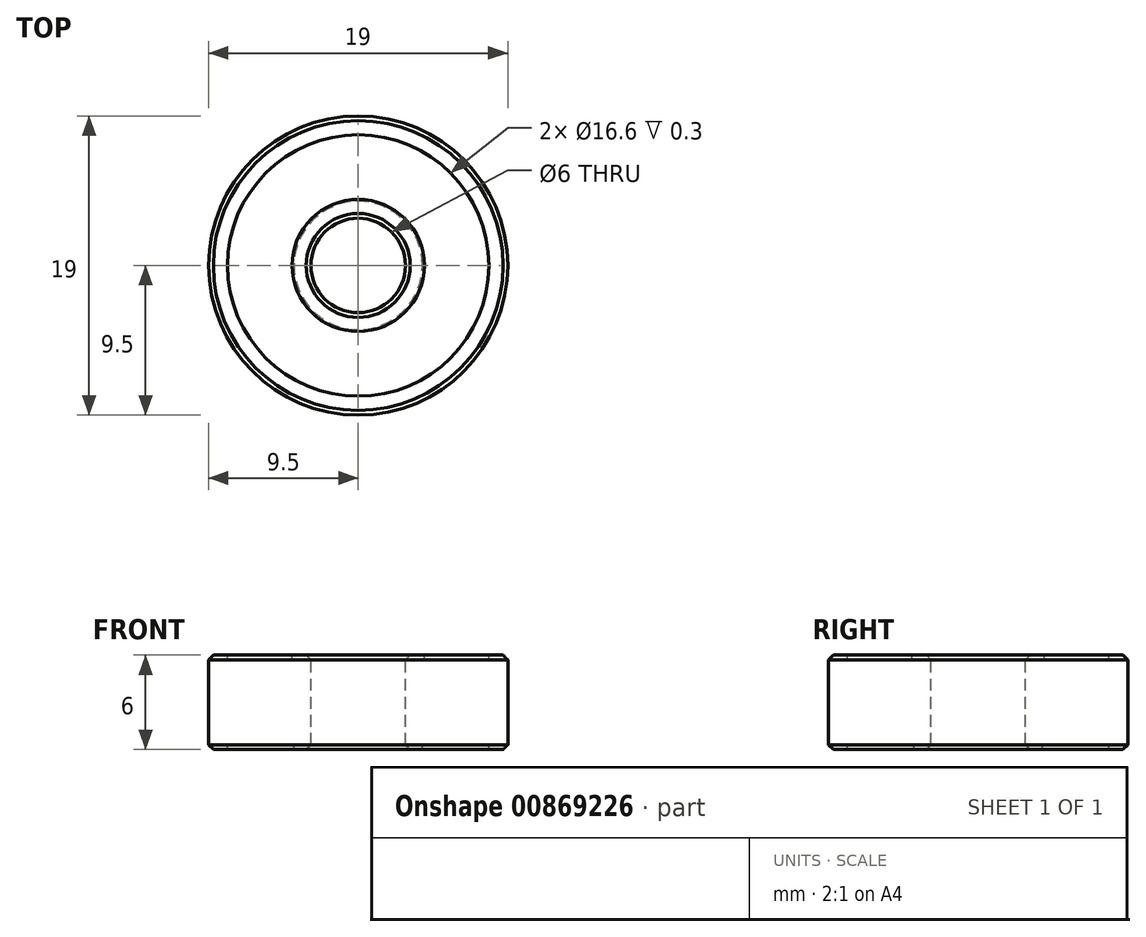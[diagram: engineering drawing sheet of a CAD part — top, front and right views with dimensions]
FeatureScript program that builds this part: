
annotation { "Feature Type Name" : "Feature", "Feature Type Description" : "" }
export const myFeature = defineFeature(function(context is Context, id is Id, definition is map)
    precondition{}
    {
        {
            var Q0;
            Q0=qCreatedBy(makeId("Front.planeOp"),FACE);
            var sketch = newSketch(context, id + "F0", { "sketchPlane" : qUnion([Q0])});
            skLineSegment(sketch, "E0.bottom", {"start": v(3, 3) * mm, "end": v(9.5, 3) * mm});
            skLineSegment(sketch, "E0.top", {"start": v(3, -3) * mm, "end": v(9.5, -3) * mm});
            skLineSegment(sketch, "E0.left", {"start": v(3, 3) * mm, "end": v(3, -3) * mm});
            skLineSegment(sketch, "E0.right", {"start": v(9.5, 3) * mm, "end": v(9.5, -3) * mm});
            skLineSegment(sketch, "E1", {"start": v(0, 3) * mm, "end": v(0, -3) * mm, "construction": true});
            skLineSegment(sketch, "E2", {"start": v(4.2, 3) * mm, "end": v(4.2, 2.7) * mm});
            skLineSegment(sketch, "E3", {"start": v(4.2, 2.7) * mm, "end": v(8.3, 2.7) * mm});
            skLineSegment(sketch, "E4", {"start": v(8.3, 2.7) * mm, "end": v(8.3, 3) * mm});
            skLineSegment(sketch, "E5", {"start": v(4.08, -3) * mm, "end": v(4.08, -2.7) * mm});
            skLineSegment(sketch, "E6", {"start": v(4.08, -2.7) * mm, "end": v(8.3, -2.7) * mm});
            skLineSegment(sketch, "E7", {"start": v(8.3, -2.7) * mm, "end": v(8.3, -3) * mm});
            skSolve(sketch);
        }
        {
            var Q0;
            {var subQ3=sQuery(id+"F0.wireOp",EDGE,"E0.left");Q0=makeQuery(id+"F0.imprint","IMPRINT",FACE,{"disambiguationData":[TD([[makeQuery(id+"F0.imprint","IMPRINT",EDGE,{"derivedFrom":subQ3}),1.0]])]});}
            var Q1;
            Q1=sQuery(id+"F0.wireOp",EDGE,"E1");
            revolve(context, id + "F1", {"surfaceOperationType" : NewSurfaceOperationType.NEW, "entities" : qUnion([Q0]), "axis" : qUnion([Q1]), "revolveType" : RevolveType.FULL});
        }
        {
            var Q0;
            Q0=makeQuery(id+"F1.opRevolve","SWEPT_EDGE",EDGE,{"disambiguationData":[OSD([sQuery(id+"F0.wireOp",EDGE,"E0.bottom"),sQuery(id+"F0.wireOp",EDGE,"E0.right")])]});
            var Q1;
            Q1=makeQuery(id+"F1.opRevolve","SWEPT_EDGE",EDGE,{"disambiguationData":[OSD([sQuery(id+"F0.wireOp",EDGE,"E0.top"),sQuery(id+"F0.wireOp",EDGE,"E0.right")])]});
            var Q2;
            Q2=makeQuery(id+"F1.opRevolve","SWEPT_EDGE",EDGE,{"disambiguationData":[OSD([sQuery(id+"F0.wireOp",EDGE,"E0.bottom"),sQuery(id+"F0.wireOp",EDGE,"E0.left")])]});
            var Q3;
            Q3=makeQuery(id+"F1.opRevolve","SWEPT_EDGE",EDGE,{"disambiguationData":[OSD([sQuery(id+"F0.wireOp",EDGE,"E0.top"),sQuery(id+"F0.wireOp",EDGE,"E0.left")])]});
            chamfer(context, id + "F2", {"entities" : qUnion([Q0, Q1, Q2, Q3]), "width" : 0.3 * mm, "tangentPropagation" : true});
        }
    });
